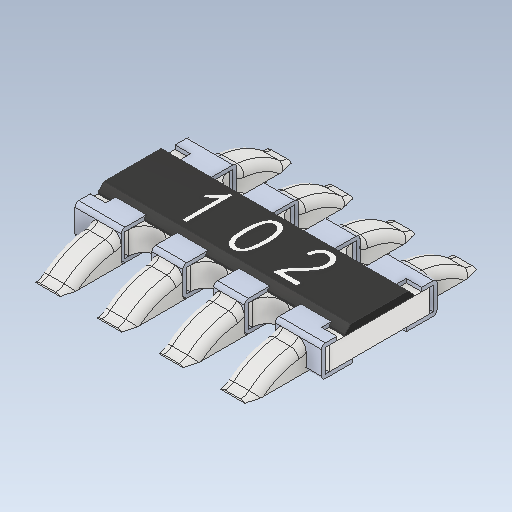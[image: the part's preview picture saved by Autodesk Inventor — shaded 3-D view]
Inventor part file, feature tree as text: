
AUTODESK INVENTOR PART (.ipt)
format: ipt  version: 2020.1 (Build 241239000, 239)  size: 557,568 bytes
history: native  units: mm
features: other x8, fillet x2
ambient origin geometry x8: Origin, YZ Plane, XZ Plane, XY Plane, X Axis, Y Axis, Z Axis, Center Point
bodies: Solid1 (feature_tree), Solid2 (feature_tree), Solid3 (feature_tree), Solid4 (feature_tree), Solid5 (feature_tree), Solid6 (feature_tree), Solid7 (feature_tree), Solid8 (feature_tree), Solid9 (feature_tree), Solid10 (feature_tree)
feature tree (10):
  other  "Cut-Extrude7"
  other  "Boss-Extrude5"
  fillet  "Fillet2"  [1 undecoded]
  fillet  "Fillet1"  [1 undecoded]
  other  "LPattern3[1]"
  other  "LPattern3[2]"
  other  "LPattern3[3]"
  other  "LPattern3[4]"
  other  "LPattern3[5]"
  other  "LPattern3[6]"
note: 2 required parameter values undecoded (feature->parameter linkage not recoverable at this tier; creation-order binding heuristic only, values carry confidence <= 0.55)
